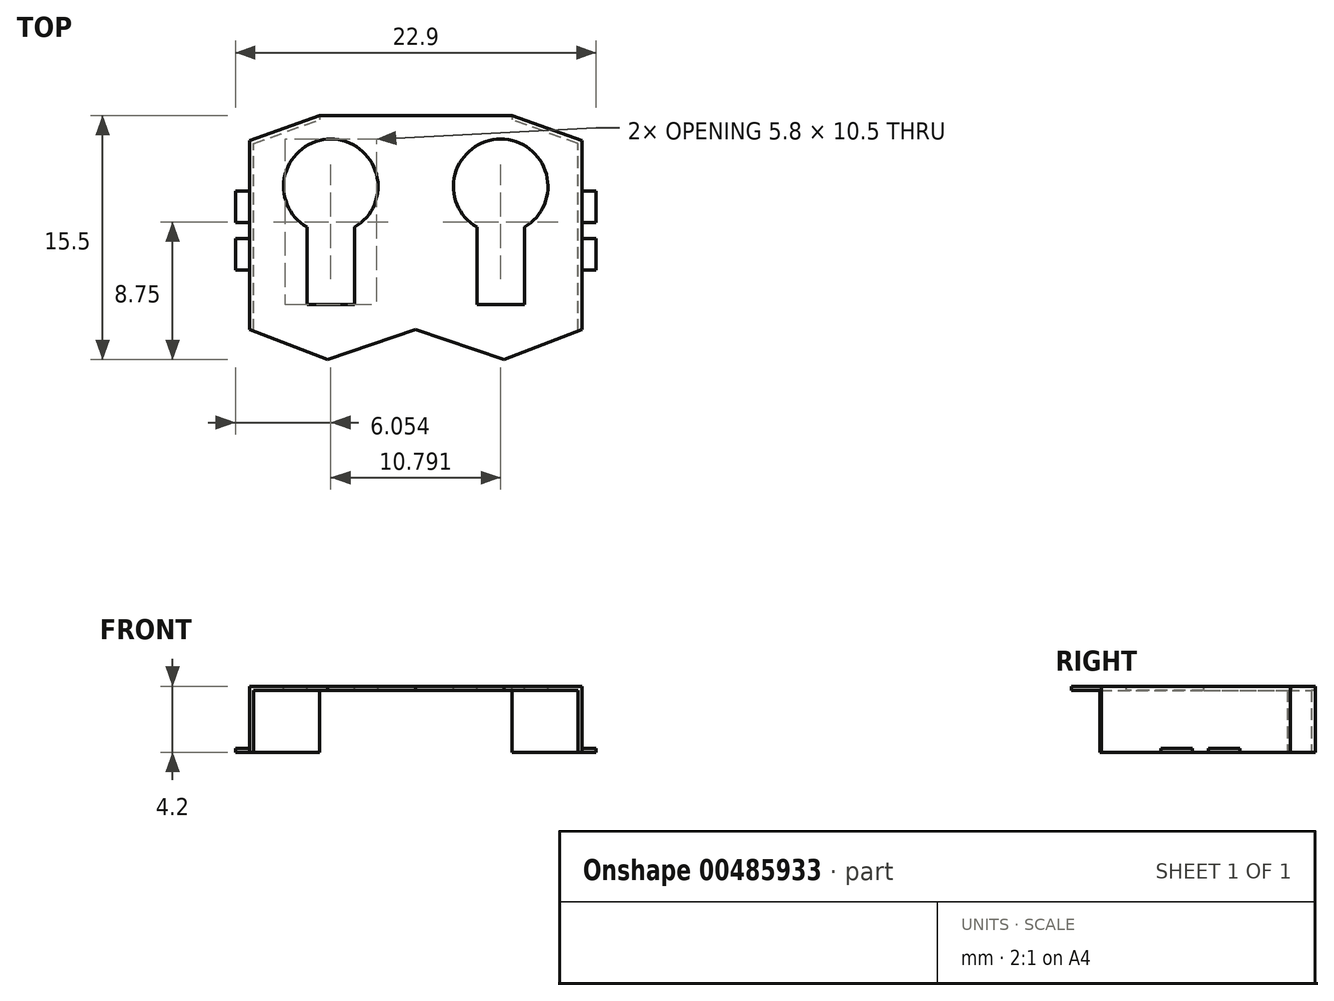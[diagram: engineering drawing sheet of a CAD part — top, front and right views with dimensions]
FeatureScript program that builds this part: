
annotation { "Feature Type Name" : "Feature", "Feature Type Description" : "" }
export const myFeature = defineFeature(function(context is Context, id is Id, definition is map)
    precondition{}
    {
        {
            var Q0;
            Q0=qCreatedBy(makeId("Top.planeOp"),FACE);
            var sketch = newSketch(context, id + "F0", { "sketchPlane" : qUnion([Q0])});
            skLineSegment(sketch, "E0", {"start": v(-10.55, 5.2) * mm, "end": v(-6.1, 6.8) * mm});
            skLineSegment(sketch, "E1", {"start": v(-10.55, 5.2) * mm, "end": v(-10.55, 2) * mm});
            skLineSegment(sketch, "E2", {"start": v(-10.55, 2) * mm, "end": v(-11.45, 2) * mm});
            skLineSegment(sketch, "E3", {"start": v(-11.45, 2) * mm, "end": v(-11.45, 0) * mm});
            skLineSegment(sketch, "E4", {"start": v(-11.45, 0) * mm, "end": v(-10.55, 0) * mm});
            skLineSegment(sketch, "E5", {"start": v(-10.55, 0) * mm, "end": v(-10.55, -1) * mm});
            skLineSegment(sketch, "E6", {"start": v(-10.55, -1) * mm, "end": v(-11.45, -1) * mm});
            skLineSegment(sketch, "E7", {"start": v(-11.45, -1) * mm, "end": v(-11.45, -3) * mm});
            skLineSegment(sketch, "E8", {"start": v(-11.45, -3) * mm, "end": v(-10.55, -3) * mm});
            skLineSegment(sketch, "E9", {"start": v(0, -6.8) * mm, "end": v(0, 0) * mm});
            skLineSegment(sketch, "E10", {"start": v(0, 0) * mm, "end": v(0, 6.8) * mm});
            skLineSegment(sketch, "E11", {"start": v(0, 6.8) * mm, "end": v(-6.1, 6.8) * mm});
            skLineSegment(sketch, "E12", {"start": v(-10.55, -6.8) * mm, "end": v(-5.6, -8.7) * mm});
            skLineSegment(sketch, "E13", {"start": v(-5.6, -8.7) * mm, "end": v(0, -6.8) * mm});
            skLineSegment(sketch, "E14", {"start": v(-10.55, -3) * mm, "end": v(-10.55, -6.8) * mm});
            skLineSegment(sketch, "E15.MirrorCS", {"start": v(0, 6.8) * mm, "end": v(6.1, 6.8) * mm});
            skLineSegment(sketch, "E16.MirrorCS", {"start": v(10.55, 5.2) * mm, "end": v(6.1, 6.8) * mm});
            skLineSegment(sketch, "E17.MirrorCS", {"start": v(10.55, 5.2) * mm, "end": v(10.55, 2) * mm});
            skLineSegment(sketch, "E18.MirrorCS", {"start": v(10.55, 2) * mm, "end": v(11.45, 2) * mm});
            skLineSegment(sketch, "E19.MirrorCS", {"start": v(11.45, 2) * mm, "end": v(11.45, 0) * mm});
            skLineSegment(sketch, "E20.MirrorCS", {"start": v(10.55, 0) * mm, "end": v(10.55, -1) * mm});
            skLineSegment(sketch, "E21.MirrorCS", {"start": v(11.45, 0) * mm, "end": v(10.55, 0) * mm});
            skLineSegment(sketch, "E22.MirrorCS", {"start": v(10.55, -1) * mm, "end": v(11.45, -1) * mm});
            skLineSegment(sketch, "E23.MirrorCS", {"start": v(11.45, -1) * mm, "end": v(11.45, -3) * mm});
            skLineSegment(sketch, "E24.MirrorCS", {"start": v(11.45, -3) * mm, "end": v(10.55, -3) * mm});
            skLineSegment(sketch, "E25.MirrorCS", {"start": v(10.55, -3) * mm, "end": v(10.55, -6.8) * mm});
            skLineSegment(sketch, "E26.MirrorCS", {"start": v(10.55, -6.8) * mm, "end": v(5.6, -8.7) * mm});
            skLineSegment(sketch, "E27.MirrorCS", {"start": v(5.6, -8.7) * mm, "end": v(0, -6.8) * mm});
            skCircle(sketch, "E28", {"center": v(-5.4, 2.3) * mm, "radius": 3 * mm});
            skLineSegment(sketch, "E29.bottom", {"start": v(-5.4, 2.3) * mm, "end": v(-6.9, 2.3) * mm});
            skLineSegment(sketch, "E29.top", {"start": v(-5.4, -5.2) * mm, "end": v(-6.9, -5.2) * mm});
            skLineSegment(sketch, "E29.right", {"start": v(-6.9, 2.3) * mm, "end": v(-6.9, -5.2) * mm});
            skLineSegment(sketch, "E30.MirrorCS", {"start": v(-3.9, 2.3) * mm, "end": v(-3.9, -5.2) * mm});
            skLineSegment(sketch, "E31.MirrorCS", {"start": v(-5.4, 2.3) * mm, "end": v(-3.9, 2.3) * mm});
            skLineSegment(sketch, "E32.MirrorCS", {"start": v(-5.4, -5.2) * mm, "end": v(-3.9, -5.2) * mm});
            skCircle(sketch, "E33.MirrorC", {"center": v(5.4, 2.3) * mm, "radius": 3 * mm});
            skLineSegment(sketch, "E34.MirrorCS", {"start": v(3.9, 2.3) * mm, "end": v(3.9, -5.2) * mm});
            skLineSegment(sketch, "E35.MirrorCS", {"start": v(5.4, 2.3) * mm, "end": v(3.9, 2.3) * mm});
            skLineSegment(sketch, "E36.MirrorCS", {"start": v(5.4, 2.3) * mm, "end": v(6.9, 2.3) * mm});
            skLineSegment(sketch, "E37.MirrorCS", {"start": v(6.9, 2.3) * mm, "end": v(6.9, -5.2) * mm});
            skLineSegment(sketch, "E38.MirrorCS", {"start": v(5.4, -5.2) * mm, "end": v(6.9, -5.2) * mm});
            skLineSegment(sketch, "E39.MirrorCS", {"start": v(5.4, -5.2) * mm, "end": v(3.9, -5.2) * mm});
            skSolve(sketch);
        }
        {
            var Q0;
            Q0 = qSketchRegion(id + "F0", true);
            extrude(context, id + "F1", {"entities" : qUnion([Q0]), "depth" : -4.2 * mm});
        }
        {
            var Q0;
            Q0=makeQuery(id+"F1.opExtrude","CAP_FACE",FACE,{"disambiguationData":[OSD([sQuery(id+"F0.wireOp",EDGE,"E0"),sQuery(id+"F0.wireOp",EDGE,"E1"),sQuery(id+"F0.wireOp",EDGE,"E2"),sQuery(id+"F0.wireOp",EDGE,"E3"),sQuery(id+"F0.wireOp",EDGE,"E4"),sQuery(id+"F0.wireOp",EDGE,"E5"),sQuery(id+"F0.wireOp",EDGE,"E6"),sQuery(id+"F0.wireOp",EDGE,"E7"),sQuery(id+"F0.wireOp",EDGE,"E8"),sQuery(id+"F0.wireOp",EDGE,"E11"),sQuery(id+"F0.wireOp",EDGE,"E12"),sQuery(id+"F0.wireOp",EDGE,"E13"),sQuery(id+"F0.wireOp",EDGE,"E14"),sQuery(id+"F0.wireOp",EDGE,"E15.MirrorCS"),sQuery(id+"F0.wireOp",EDGE,"E16.MirrorCS"),sQuery(id+"F0.wireOp",EDGE,"E17.MirrorCS"),sQuery(id+"F0.wireOp",EDGE,"E18.MirrorCS"),sQuery(id+"F0.wireOp",EDGE,"E19.MirrorCS"),sQuery(id+"F0.wireOp",EDGE,"E20.MirrorCS"),sQuery(id+"F0.wireOp",EDGE,"E21.MirrorCS"),sQuery(id+"F0.wireOp",EDGE,"E22.MirrorCS"),sQuery(id+"F0.wireOp",EDGE,"E23.MirrorCS"),sQuery(id+"F0.wireOp",EDGE,"E24.MirrorCS"),sQuery(id+"F0.wireOp",EDGE,"E25.MirrorCS"),sQuery(id+"F0.wireOp",EDGE,"E26.MirrorCS"),sQuery(id+"F0.wireOp",EDGE,"E27.MirrorCS")])],"isStart":false});
            var sketch = newSketch(context, id + "F2", { "sketchPlane" : qUnion([Q0])});
            skLineSegment(sketch, "E40", {"start": v(10.3, 9.38) * mm, "end": v(10.3, -5.02) * mm});
            skLineSegment(sketch, "E41", {"start": v(0, 9.38) * mm, "end": v(10.3, 9.38) * mm});
            skLineSegment(sketch, "E42", {"start": v(6.1, -8.54) * mm, "end": v(0, -8.73) * mm});
            skLineSegment(sketch, "E43", {"start": v(10.3, -5.02) * mm, "end": v(6.1, -6.53) * mm});
            skLineSegment(sketch, "E44", {"start": v(6.1, -8.54) * mm, "end": v(6.1, -6.53) * mm});
            skLineSegment(sketch, "E45.MirrorCS", {"start": v(-6.1, -8.54) * mm, "end": v(0, -8.73) * mm});
            skLineSegment(sketch, "E46.MirrorCS", {"start": v(-6.1, -8.54) * mm, "end": v(-6.1, -6.54) * mm});
            skLineSegment(sketch, "E47.MirrorCS", {"start": v(-10.3, -5.02) * mm, "end": v(-6.1, -6.54) * mm});
            skLineSegment(sketch, "E48.MirrorCS", {"start": v(-10.3, 9.38) * mm, "end": v(-10.3, -5.02) * mm});
            skLineSegment(sketch, "E49.MirrorCS", {"start": v(0, 9.38) * mm, "end": v(-10.3, 9.38) * mm});
            skSolve(sketch);
        }
        {
            var Q0;
            Q0 = qSketchRegion(id + "F2", true);
            extrude(context, id + "F3", {"entities" : qUnion([Q0]), "operationType" : NewBodyOperationType.REMOVE, "oppositeDirection" : true, "depth" : (4.2 - 0.25) * mm});
        }
        {
            var Q0;
            Q0=makeQuery(id+"F1.opExtrude","SWEPT_FACE",FACE,{"disambiguationData":[OSD([sQuery(id+"F0.wireOp",EDGE,"E8")])]});
            var sketch = newSketch(context, id + "F4", { "sketchPlane" : qUnion([Q0])});
            skLineSegment(sketch, "E50.bottom", {"start": v(-11.45, 0) * mm, "end": v(-10.55, 0) * mm});
            skLineSegment(sketch, "E50.top", {"start": v(-11.45, -3.95) * mm, "end": v(-10.55, -3.95) * mm});
            skLineSegment(sketch, "E50.left", {"start": v(-11.45, 0) * mm, "end": v(-11.45, -3.95) * mm});
            skLineSegment(sketch, "E50.right", {"start": v(-10.55, 0) * mm, "end": v(-10.55, -3.95) * mm});
            skLineSegment(sketch, "E51.MirrorCS", {"start": v(11.45, 0) * mm, "end": v(11.45, -3.95) * mm});
            skLineSegment(sketch, "E52.MirrorCS", {"start": v(10.55, 0) * mm, "end": v(10.55, -3.95) * mm});
            skLineSegment(sketch, "E53.MirrorCS", {"start": v(11.45, -3.95) * mm, "end": v(10.55, -3.95) * mm});
            skLineSegment(sketch, "E54.MirrorCS", {"start": v(11.45, 0) * mm, "end": v(10.55, 0) * mm});
            skSolve(sketch);
        }
        {
            var Q0;
            Q0 = qSketchRegion(id + "F4", true);
            extrude(context, id + "F5", {"entities" : qUnion([Q0]), "operationType" : NewBodyOperationType.REMOVE, "endBound" : BoundingType.THROUGH_ALL, "oppositeDirection" : true, "depth" : 25 * mm});
        }
    });
